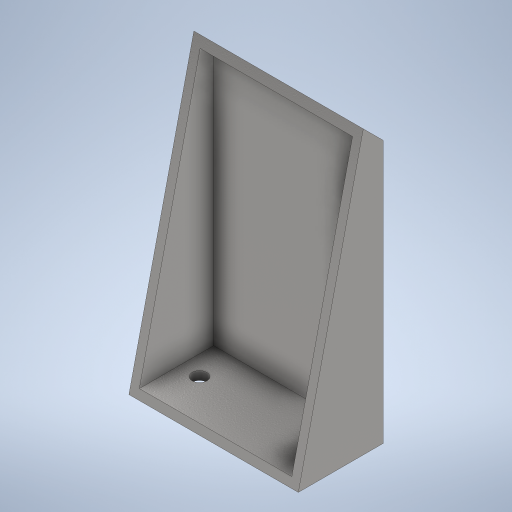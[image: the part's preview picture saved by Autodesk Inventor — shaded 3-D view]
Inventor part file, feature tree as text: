
AUTODESK INVENTOR PART (.ipt)
format: ipt  version: 2024.2 (Build 282272000, 272)  size: 279,040 bytes
history: native  units: mm
features: extrude x3, sketch x3, chamfer x1, shell x1
ambient origin geometry x8: Origin, YZ Plane, XZ Plane, XY Plane, X Axis, Y Axis, Z Axis, Center Point
bodies: Body1 (feature_tree)
feature tree (8):
  extrude  "Extrusion4"  Depth=30.0mm
  chamfer  "Chamfer1"  Distance=100.0mm
  extrude  "Extrusion5"  Depth=3.0mm TaperAngle=0.0deg
  shell  "Shell2"  Thickness=3.0mm
  extrude  "Extrusion6"  Depth=20.0mm
  sketch  "Sketch4"  dims[d15=60.0mm d16=30.0mm d17=100.0mm d18=0.0mm]
  sketch  "Sketch6"  dims[d19=7.0mm d20=2.0mm d21=45.0deg d22=100.0mm d23=0.0mm d25=3.0mm]
  sketch  "Sketch8"  dims[d26=15.0mm d27=20.0mm d28=5.2mm d29=20.0mm d30=0.0mm d3=0.5mm d4=0.872665mm d5=0.5mm d6=0.872665mm]
